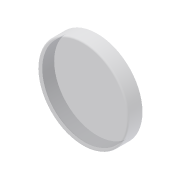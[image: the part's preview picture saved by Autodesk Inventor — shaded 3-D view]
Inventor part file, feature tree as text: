
AUTODESK INVENTOR PART (.ipt)
format: ipt  version: 2014 (Build 180170000, 170)  size: 121,344 bytes
history: native  units: mm
features: extrude x2, sketch x2, fillet x1
ambient origin geometry x8: Origin, YZ Plane, XZ Plane, XY Plane, X Axis, Y Axis, Z Axis, Center Point
bodies: Solid1 (feature_tree)
feature tree (5):
  extrude  "Extrusion1"  Depth=2.0mm TaperAngle=0.0deg
  extrude  "Extrusion2"  Depth=2.0mm
  fillet  "Fillet1"  Radius=120.0mm
  sketch  "Sketch1"  dims[d0=100.0mm d1=2.0mm d2=0.0mm]
  sketch  "Sketch2"  dims[d5=17.0mm d6=0.0mm d7=2.0mm d8=120.0mm d9=3.0mm]
